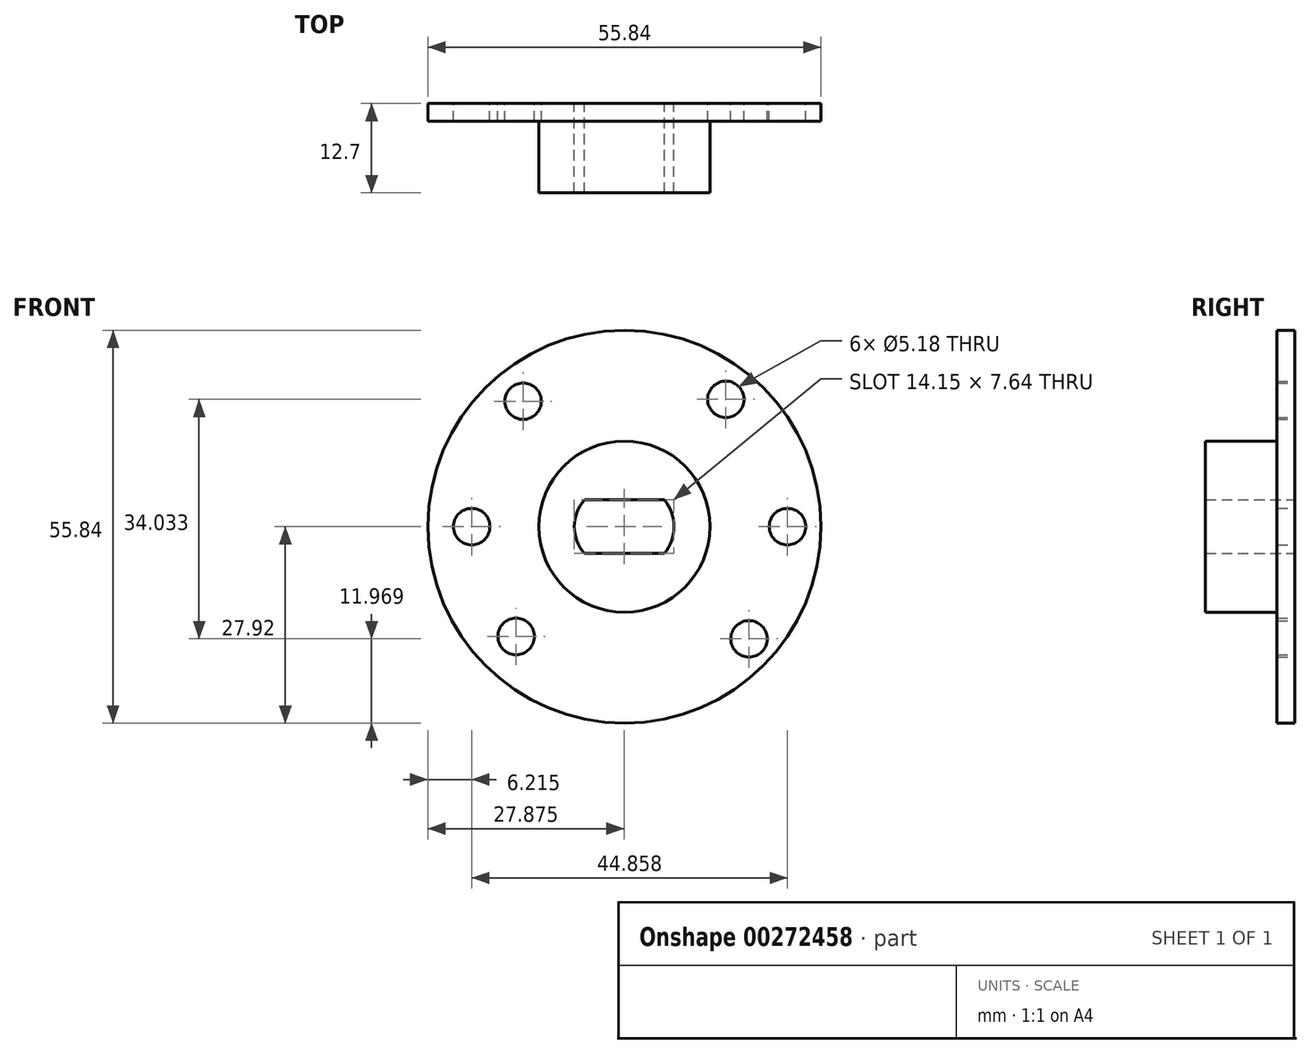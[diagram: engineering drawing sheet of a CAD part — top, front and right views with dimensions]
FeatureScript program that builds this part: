
annotation { "Feature Type Name" : "Feature", "Feature Type Description" : "" }
export const myFeature = defineFeature(function(context is Context, id is Id, definition is map)
    precondition{}
    {
        {
            var Q0;
            Q0=qCreatedBy(makeId("Front.planeOp"),FACE);
            var sketch = newSketch(context, id + "F0", { "sketchPlane" : qUnion([Q0])});
            skCircle(sketch, "E0", {"center": v(0, 0) * mm, "radius": 27.92 * mm});
            skCircle(sketch, "E1", {"center": v(-21.7, 0) * mm, "radius": 2.6 * mm});
            skCircle(sketch, "E2", {"center": v(-15.38, -15.6) * mm, "radius": 2.6 * mm});
            skCircle(sketch, "E3", {"center": v(17.7, -15.95) * mm, "radius": 2.6 * mm});
            skCircle(sketch, "E4", {"center": v(23.15, 0) * mm, "radius": 2.6 * mm});
            skCircle(sketch, "E5", {"center": v(14.4, 18.08) * mm, "radius": 2.6 * mm});
            skCircle(sketch, "E6", {"center": v(0, 0) * mm, "radius": 12.17 * mm});
            skLineSegment(sketch, "E7.bottom", {"start": v(5.7, -3.82) * mm, "end": v(-5.7, -3.82) * mm});
            skLineSegment(sketch, "E7.top", {"start": v(5.7, 3.82) * mm, "end": v(-5.7, 3.82) * mm});
            skArc(sketch, "E8", {"start": v(5.7, -3.82) * mm, "mid": v(7.03, 0) * mm, "end": v(5.7, 3.82) * mm});
            skArc(sketch, "E9", {"start": v(-5.7, 3.82) * mm, "mid": v(-7.12, 0) * mm, "end": v(-5.7, -3.82) * mm});
            skCircle(sketch, "E10", {"center": v(-14.4, 17.82) * mm, "radius": 2.6 * mm});
            skLineSegment(sketch, "E11.bottom", {"start": v(-2.88, -3.82) * mm, "end": v(2.95, -3.82) * mm});
            skLineSegment(sketch, "E11.left", {"start": v(-2.88, -3.82) * mm, "end": v(-2.88, -11.8) * mm});
            skLineSegment(sketch, "E11.right", {"start": v(2.95, -3.82) * mm, "end": v(2.95, -11.8) * mm});
            skSolve(sketch);
        }
        {
            var Q0;
            Q0 = qSketchRegion(id + "F0", true);
            var Q1;
            Q1=makeQuery(id+"F0.imprint","IMPRINT",FACE,{"disambiguationData":[TD([[makeQuery(id+"F0.imprint","IMPRINT",EDGE,{"derivedFrom":sQuery(id+"F0.wireOp",EDGE,"E6")}),1.0]])]});
            extrude(context, id + "F1", {"entities" : qUnion([Q0, Q1]), "depth" : 2.54 * mm});
        }
        {
            var Q0;
            Q0=makeQuery(id+"F0.imprint","IMPRINT",FACE,{"disambiguationData":[TD([[makeQuery(id+"F0.imprint","IMPRINT",EDGE,{"derivedFrom":sQuery(id+"F0.wireOp",EDGE,"E6")}),1.0]])]});
            extrude(context, id + "F2", {"entities" : qUnion([Q0]), "operationType" : NewBodyOperationType.ADD, "depth" : 12.7 * mm});
        }
    });
